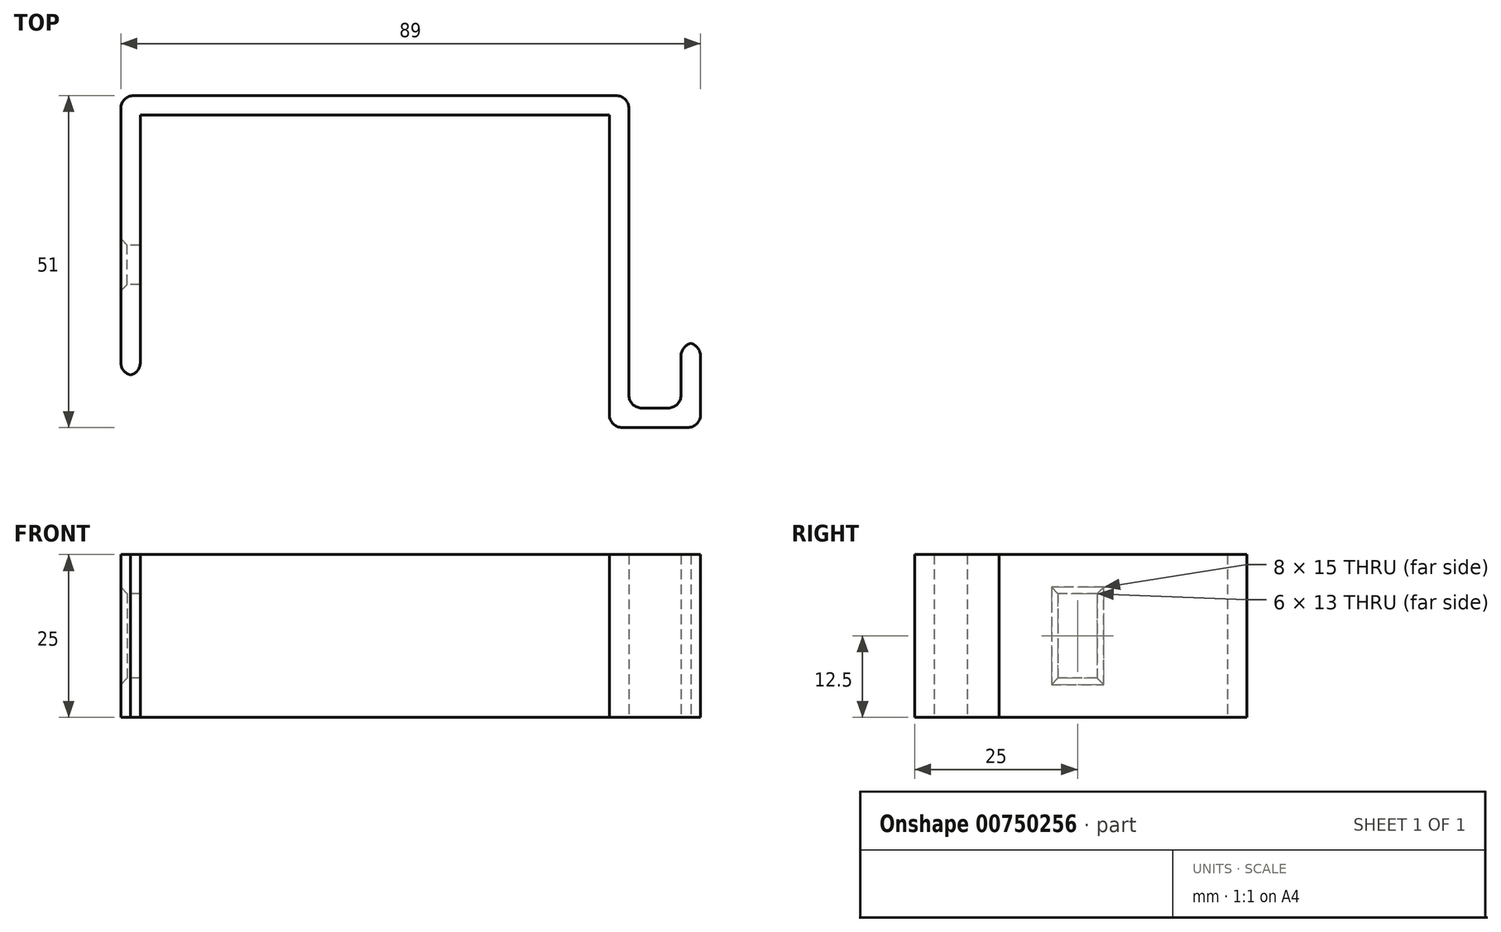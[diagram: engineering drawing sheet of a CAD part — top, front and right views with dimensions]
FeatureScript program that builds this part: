
annotation { "Feature Type Name" : "Feature", "Feature Type Description" : "" }
export const myFeature = defineFeature(function(context is Context, id is Id, definition is map)
    precondition{}
    {
        {
            var Q0;
            Q0=qCreatedBy(makeId("Top.planeOp"),FACE);
            var sketch = newSketch(context, id + "F0", { "sketchPlane" : qUnion([Q0])});
            skLineSegment(sketch, "E0", {"start": v(-52.14, -5) * mm, "end": v(-52.14, 35) * mm});
            skLineSegment(sketch, "E1", {"start": v(-52.14, 35) * mm, "end": v(19.86, 35) * mm});
            skLineSegment(sketch, "E2", {"start": v(19.86, 35) * mm, "end": v(19.86, -10) * mm});
            skLineSegment(sketch, "E3", {"start": v(22.86, -10) * mm, "end": v(30.86, -10) * mm});
            skLineSegment(sketch, "E4", {"start": v(30.86, -10) * mm, "end": v(30.86, 0) * mm});
            skLineSegment(sketch, "E5.0", {"start": v(22.86, 38) * mm, "end": v(22.86, -10) * mm});
            skLineSegment(sketch, "E5.1", {"start": v(-55.14, 38) * mm, "end": v(22.86, 38) * mm});
            skLineSegment(sketch, "E5.2", {"start": v(-55.14, -5) * mm, "end": v(-55.14, 38) * mm});
            skLineSegment(sketch, "E6", {"start": v(-52.14, -5) * mm, "end": v(-55.14, -5) * mm});
            skLineSegment(sketch, "E7.0", {"start": v(33.86, -10) * mm, "end": v(33.86, 0) * mm});
            skLineSegment(sketch, "E8", {"start": v(30.86, 0) * mm, "end": v(33.86, 0) * mm});
            skLineSegment(sketch, "E9.0", {"start": v(19.86, -13) * mm, "end": v(30.86, -13) * mm});
            skLineSegment(sketch, "E10", {"start": v(30.86, -13) * mm, "end": v(33.86, -13) * mm});
            skLineSegment(sketch, "E11", {"start": v(33.86, -10) * mm, "end": v(33.86, -13) * mm});
            skLineSegment(sketch, "E12", {"start": v(19.86, -10) * mm, "end": v(19.86, -13) * mm});
            skSolve(sketch);
        }
        {
            var Q0;
            Q0 = qSketchRegion(id + "F0", true);
            extrude(context, id + "F1", {"entities" : qUnion([Q0]), "depth" : 25 * mm, "offsetDistance" : 25 * mm});
        }
        {
            var Q0;
            Q0=makeQuery(id+"F1.opExtrude","SWEPT_FACE",FACE,{"disambiguationData":[OSD([sQuery(id+"F0.wireOp",EDGE,"E5.2")])]});
            var sketch = newSketch(context, id + "F2", { "sketchPlane" : qUnion([Q0])});
            skLineSegment(sketch, "E13.bottom", {"start": v(-15, 19) * mm, "end": v(-9, 19) * mm});
            skLineSegment(sketch, "E13.top", {"start": v(-15, 6) * mm, "end": v(-9, 6) * mm});
            skLineSegment(sketch, "E13.left", {"start": v(-15, 19) * mm, "end": v(-15, 6) * mm});
            skLineSegment(sketch, "E13.right", {"start": v(-9, 19) * mm, "end": v(-9, 6) * mm});
            skSolve(sketch);
        }
        {
            var Q0;
            Q0=makeQuery(id+"F2.imprint","IMPRINT",FACE,{"disambiguationData":[TD([[makeQuery(id+"F2.imprint","IMPRINT",EDGE,{"derivedFrom":sQuery(id+"F2.wireOp",EDGE,"E13.bottom")}),-1.0]])]});
            extrude(context, id + "F3", {"entities" : qUnion([Q0]), "operationType" : NewBodyOperationType.REMOVE, "endBound" : BoundingType.SYMMETRIC, "oppositeDirection" : true, "depth" : 25 * mm, "offsetDistance" : 25 * mm});
        }
        {
            var Q0;
            Q0=makeQuery(id+"F3.boolean.opBoolean","INTERSECT",EDGE,{"derivedFrom":[makeQuery(id+"F1.opExtrude","SWEPT_FACE",FACE,{"disambiguationData":[OSD([sQuery(id+"F0.wireOp",EDGE,"E5.2")])]}),makeQuery(id+"F3.opExtrude","SWEPT_FACE",FACE,{"disambiguationData":[OSD([sQuery(id+"F2.wireOp",EDGE,"E13.bottom")])]})]});
            var Q1;
            Q1=makeQuery(id+"F3.boolean.opBoolean","INTERSECT",EDGE,{"derivedFrom":[makeQuery(id+"F1.opExtrude","SWEPT_FACE",FACE,{"disambiguationData":[OSD([sQuery(id+"F0.wireOp",EDGE,"E5.2")])]}),makeQuery(id+"F3.opExtrude","SWEPT_FACE",FACE,{"disambiguationData":[OSD([sQuery(id+"F2.wireOp",EDGE,"E13.left")])]})]});
            var Q2;
            Q2=makeQuery(id+"F3.boolean.opBoolean","INTERSECT",EDGE,{"derivedFrom":[makeQuery(id+"F1.opExtrude","SWEPT_FACE",FACE,{"disambiguationData":[OSD([sQuery(id+"F0.wireOp",EDGE,"E5.2")])]}),makeQuery(id+"F3.opExtrude","SWEPT_FACE",FACE,{"disambiguationData":[OSD([sQuery(id+"F2.wireOp",EDGE,"E13.right")])]})]});
            var Q3;
            Q3=makeQuery(id+"F3.boolean.opBoolean","INTERSECT",EDGE,{"derivedFrom":[makeQuery(id+"F1.opExtrude","SWEPT_FACE",FACE,{"disambiguationData":[OSD([sQuery(id+"F0.wireOp",EDGE,"E5.2")])]}),makeQuery(id+"F3.opExtrude","SWEPT_FACE",FACE,{"disambiguationData":[OSD([sQuery(id+"F2.wireOp",EDGE,"E13.top")])]})]});
            chamfer(context, id + "F4", {"entities" : qUnion([Q0, Q1, Q2, Q3]), "chamferType" : ChamferType.TWO_OFFSETS, "width1" : 1 * mm, "oppositeDirection" : false, "width2" : 1 * mm, "tangentPropagation" : true});
        }
        {
            var Q0;
            Q0=makeQuery(id+"F1.opExtrude","SWEPT_EDGE",EDGE,{"disambiguationData":[OSD([sQuery(id+"F0.wireOp",EDGE,"E5.1"),sQuery(id+"F0.wireOp",EDGE,"E5.2")])]});
            var Q1;
            Q1=makeQuery(id+"F1.opExtrude","SWEPT_EDGE",EDGE,{"disambiguationData":[OSD([sQuery(id+"F0.wireOp",EDGE,"E5.0"),sQuery(id+"F0.wireOp",EDGE,"E5.1")])]});
            var Q2;
            Q2=makeQuery(id+"F1.opExtrude","SWEPT_EDGE",EDGE,{"disambiguationData":[OSD([sQuery(id+"F0.wireOp",EDGE,"E9.0"),sQuery(id+"F0.wireOp",EDGE,"E12")])]});
            var Q3;
            Q3=makeQuery(id+"F1.opExtrude","SWEPT_EDGE",EDGE,{"disambiguationData":[OSD([sQuery(id+"F0.wireOp",EDGE,"E10"),sQuery(id+"F0.wireOp",EDGE,"E11")])]});
            var Q4;
            Q4=makeQuery(id+"F1.opExtrude","SWEPT_EDGE",EDGE,{"disambiguationData":[OSD([sQuery(id+"F0.wireOp",EDGE,"E7.0"),sQuery(id+"F0.wireOp",EDGE,"E8")])]});
            var Q5;
            Q5=makeQuery(id+"F1.opExtrude","SWEPT_EDGE",EDGE,{"disambiguationData":[OSD([sQuery(id+"F0.wireOp",EDGE,"E4"),sQuery(id+"F0.wireOp",EDGE,"E8")])]});
            var Q6;
            Q6=makeQuery(id+"F1.opExtrude","SWEPT_EDGE",EDGE,{"disambiguationData":[OSD([sQuery(id+"F0.wireOp",EDGE,"E5.0"),sQuery(id+"F0.wireOp",EDGE,"E3")])]});
            var Q7;
            Q7=makeQuery(id+"F1.opExtrude","SWEPT_EDGE",EDGE,{"disambiguationData":[OSD([sQuery(id+"F0.wireOp",EDGE,"E4"),sQuery(id+"F0.wireOp",EDGE,"E3")])]});
            var Q8;
            Q8=makeQuery(id+"F1.opExtrude","SWEPT_EDGE",EDGE,{"disambiguationData":[OSD([sQuery(id+"F0.wireOp",EDGE,"E5.2"),sQuery(id+"F0.wireOp",EDGE,"E6")])]});
            var Q9;
            Q9=makeQuery(id+"F1.opExtrude","SWEPT_EDGE",EDGE,{"disambiguationData":[OSD([sQuery(id+"F0.wireOp",EDGE,"E0"),sQuery(id+"F0.wireOp",EDGE,"E6")])]});
            fillet(context, id + "F5", {"entities" : qUnion([Q0, Q1, Q2, Q3, Q4, Q5, Q6, Q7, Q8, Q9]), "radius" : 2 * mm, "tangentPropagation" : true, "allowEdgeOverflow" : false});
        }
    });
